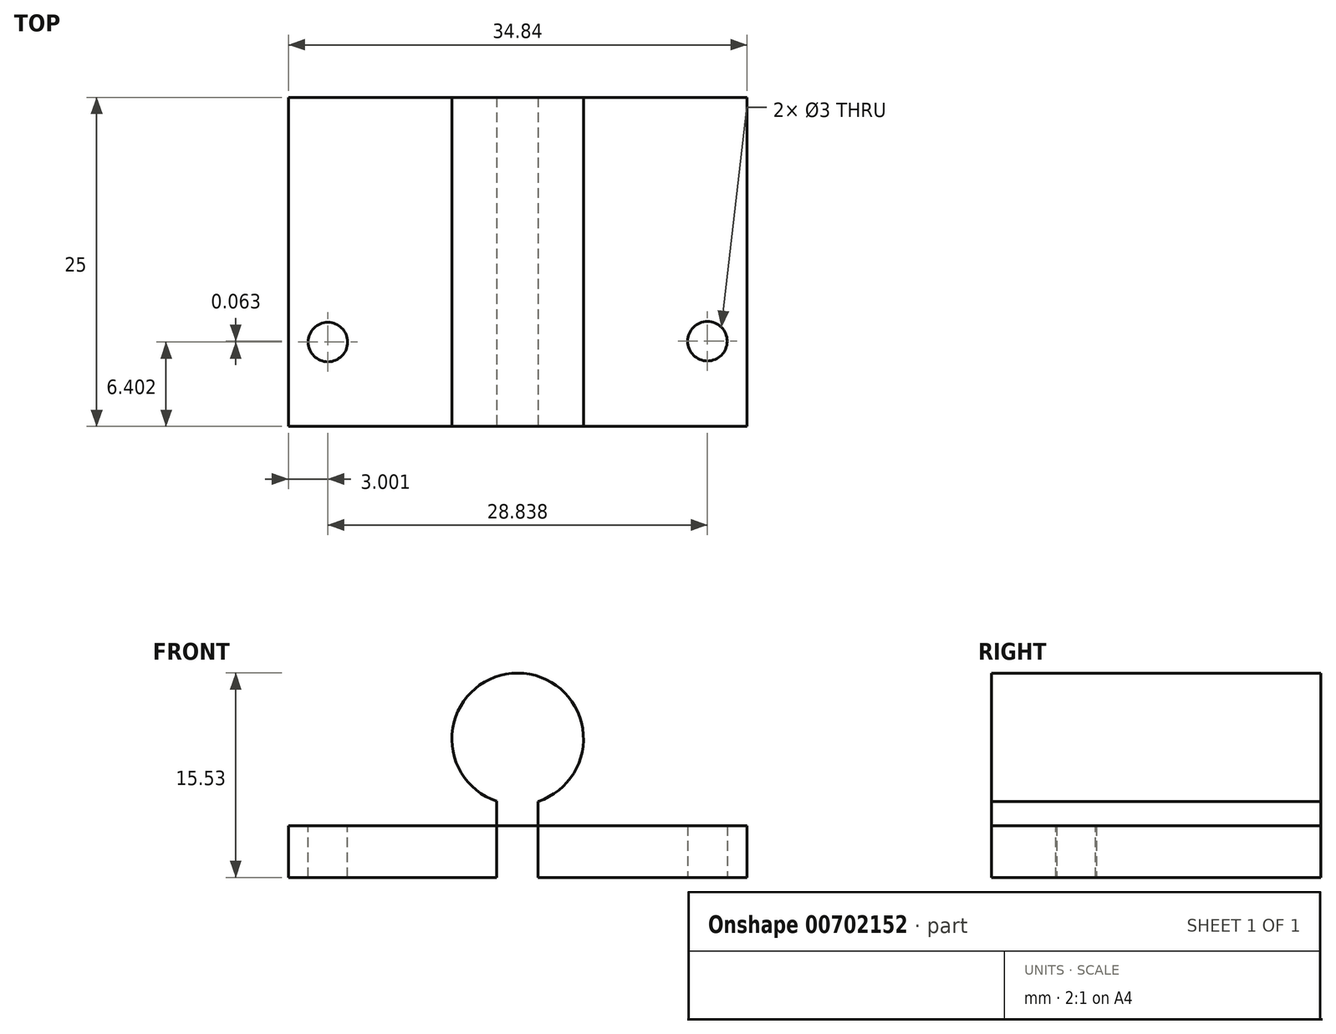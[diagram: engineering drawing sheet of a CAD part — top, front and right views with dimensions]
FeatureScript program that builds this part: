
annotation { "Feature Type Name" : "Feature", "Feature Type Description" : "" }
export const myFeature = defineFeature(function(context is Context, id is Id, definition is map)
    precondition{}
    {
        {
            var Q0;
            Q0=qCreatedBy(makeId("Front.planeOp"),FACE);
            var sketch = newSketch(context, id + "F0", { "sketchPlane" : qUnion([Q0])});
            skLineSegment(sketch, "E0.bottom", {"start": v(-17.42, 1.96) * mm, "end": v(17.42, 1.96) * mm});
            skLineSegment(sketch, "E0.top", {"start": v(-17.42, -1.96) * mm, "end": v(17.42, -1.96) * mm});
            skLineSegment(sketch, "E0.left", {"start": v(-17.42, 1.96) * mm, "end": v(-17.42, -1.96) * mm});
            skLineSegment(sketch, "E0.right", {"start": v(17.42, 1.96) * mm, "end": v(17.42, -1.96) * mm});
            skPoint(sketch, "E0.middle", {"position": v(0, 0) * mm});
            skLineSegment(sketch, "E1.bottom", {"start": v(-1.6, -1.96) * mm, "end": v(1.56, -1.96) * mm});
            skLineSegment(sketch, "E1.top", {"start": v(-1.6, 8.57) * mm, "end": v(1.56, 8.57) * mm});
            skLineSegment(sketch, "E1.left", {"start": v(-1.6, -1.96) * mm, "end": v(-1.6, 8.57) * mm});
            skLineSegment(sketch, "E1.right", {"start": v(1.56, -1.96) * mm, "end": v(1.56, 8.57) * mm});
            skCircle(sketch, "E2", {"center": v(0, 8.57) * mm, "radius": 5 * mm});
            skSolve(sketch);
        }
        {
            var Q0;
            Q0=qCreatedBy(makeId("Top.planeOp"),FACE);
            var sketch = newSketch(context, id + "F1", { "sketchPlane" : qUnion([Q0])});
            skLineSegment(sketch, "E3", {"start": v(-17.42, 0) * mm, "end": v(-17.42, 14.1) * mm});
            skLineSegment(sketch, "E4", {"start": v(17.42, 0) * mm, "end": v(17.42, 14.1) * mm});
            skLineSegment(sketch, "E5", {"start": v(-17.42, 14.1) * mm, "end": v(17.42, 14.1) * mm});
            skCircle(sketch, "E6", {"center": v(14.42, 6.47) * mm, "radius": 1.5 * mm});
            skCircle(sketch, "E7", {"center": v(-14.42, 6.4) * mm, "radius": 1.5 * mm});
            skSolve(sketch);
        }
        {
            var Q0;
            {var subQ0=sQuery(id+"F0.wireOp",EDGE,"E1.top");Q0=makeQuery(id+"F0.imprint","IMPRINT",FACE,{"disambiguationData":[TD([[makeQuery(id+"F0.imprint","IMPRINT",EDGE,{"derivedFrom":subQ0}),1.0]])]});}
            var Q1;
            {var subQ0=sQuery(id+"F0.wireOp",EDGE,"E1.top");Q1=makeQuery(id+"F0.imprint","IMPRINT",FACE,{"disambiguationData":[TD([[makeQuery(id+"F0.imprint","IMPRINT",EDGE,{"derivedFrom":subQ0}),-1.0]])]});}
            var Q2;
            {var subQ5=sQuery(id+"F0.wireOp",EDGE,"E1.bottom");Q2=makeQuery(id+"F0.imprint","IMPRINT",FACE,{"disambiguationData":[TD([[makeQuery(id+"F0.imprint","IMPRINT",EDGE,{"derivedFrom":subQ5}),1.0]])]});}
            var Q3;
            {var subQ0=sQuery(id+"F0.wireOp",EDGE,"E1.left");var subQ1=sQuery(id+"F0.wireOp",EDGE,"E0.bottom");var subQ2=makeQuery(id+"F0.imprint","INTERSECT",VERTEX,{"derivedFrom":[subQ1,subQ0]});Q3=makeQuery(id+"F0.imprint","IMPRINT",FACE,{"disambiguationData":[TD([[makeQuery(id+"F0.imprint","IMPRINT",EDGE,{"disambiguationData":[TD([[subQ2,-1.0]])],"derivedFrom":subQ1}),1.0]])]});}
            var Q4;
            {var subQ0=sQuery(id+"F0.wireOp",EDGE,"E0.right");Q4=makeQuery(id+"F0.imprint","IMPRINT",FACE,{"disambiguationData":[TD([[makeQuery(id+"F0.imprint","IMPRINT",EDGE,{"derivedFrom":subQ0}),-1.0]])]});}
            var Q5;
            {var subQ0=sQuery(id+"F0.wireOp",EDGE,"E0.left");Q5=makeQuery(id+"F0.imprint","IMPRINT",FACE,{"disambiguationData":[TD([[makeQuery(id+"F0.imprint","IMPRINT",EDGE,{"derivedFrom":subQ0}),1.0]])]});}
            extrude(context, id + "F2", {"entities" : qUnion([Q0, Q1, Q2, Q3, Q4, Q5]), "oppositeDirection" : true, "depth" : 25 * mm, "offsetDistance" : 25 * mm});
        }
        {
            var Q0;
            Q0=makeQuery(id+"F1.imprint","IMPRINT",FACE,{"disambiguationData":[TD([[makeQuery(id+"F1.imprint","IMPRINT",EDGE,{"derivedFrom":sQuery(id+"F1.wireOp",EDGE,"E6")}),1.0]])]});
            extrude(context, id + "F3", {"entities" : qUnion([Q0]), "operationType" : NewBodyOperationType.REMOVE, "endBound" : BoundingType.SYMMETRIC, "depth" : 12 * mm, "offsetDistance" : 25 * mm});
        }
        {
            var Q0;
            Q0=makeQuery(id+"F1.imprint","IMPRINT",FACE,{"disambiguationData":[TD([[makeQuery(id+"F1.imprint","IMPRINT",EDGE,{"derivedFrom":sQuery(id+"F1.wireOp",EDGE,"E7")}),1.0]])]});
            extrude(context, id + "F4", {"entities" : qUnion([Q0]), "operationType" : NewBodyOperationType.REMOVE, "endBound" : BoundingType.SYMMETRIC, "oppositeDirection" : true, "depth" : 12 * mm, "offsetDistance" : 25 * mm});
        }
    });
